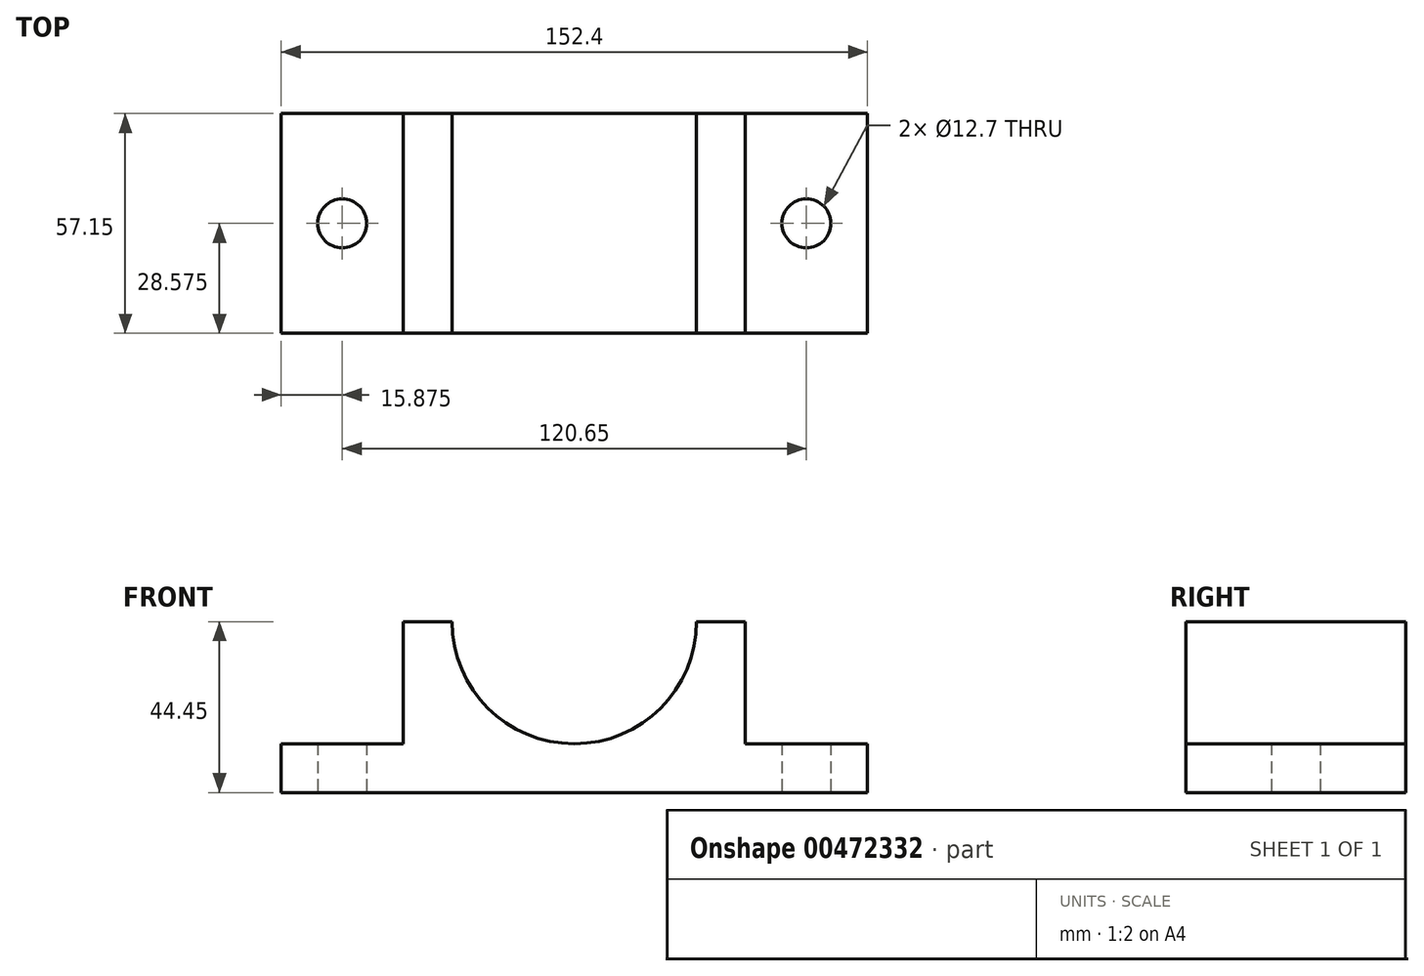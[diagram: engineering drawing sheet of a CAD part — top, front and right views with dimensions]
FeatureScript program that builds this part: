
annotation { "Feature Type Name" : "Feature", "Feature Type Description" : "" }
export const myFeature = defineFeature(function(context is Context, id is Id, definition is map)
    precondition{}
    {
        {
            var Q0;
            Q0=qCreatedBy(makeId("Front.planeOp"),FACE);
            var sketch = newSketch(context, id + "F0", { "sketchPlane" : qUnion([Q0])});
            skLineSegment(sketch, "E0", {"start": v(0, 0) * mm, "end": v(76.2, 0) * mm});
            skLineSegment(sketch, "E1", {"start": v(0, 0) * mm, "end": v(-76.2, 0) * mm});
            skLineSegment(sketch, "E2", {"start": v(76.2, 0) * mm, "end": v(76.2, 12.7) * mm});
            skLineSegment(sketch, "E3", {"start": v(-76.2, 0) * mm, "end": v(-76.2, 12.7) * mm});
            skLineSegment(sketch, "E4", {"start": v(-76.2, 12.7) * mm, "end": v(-44.45, 12.7) * mm});
            skLineSegment(sketch, "E5", {"start": v(76.2, 12.7) * mm, "end": v(44.45, 12.7) * mm});
            skLineSegment(sketch, "E6", {"start": v(-44.45, 12.7) * mm, "end": v(-44.45, 44.45) * mm});
            skLineSegment(sketch, "E7", {"start": v(44.45, 12.7) * mm, "end": v(44.45, 44.45) * mm});
            skCircle(sketch, "E8", {"center": v(0, 44.45) * mm, "radius": 31.75 * mm});
            skLineSegment(sketch, "E9", {"start": v(44.45, 44.45) * mm, "end": v(31.75, 44.45) * mm});
            skLineSegment(sketch, "E10", {"start": v(-44.45, 44.45) * mm, "end": v(-31.75, 44.45) * mm});
            skSolve(sketch);
        }
        {
            var Q0;
            Q0=makeQuery(id+"F0.imprint","IMPRINT",FACE,{"disambiguationData":[TD([[makeQuery(id+"F0.imprint","IMPRINT",EDGE,{"derivedFrom":sQuery(id+"F0.wireOp",EDGE,"E0")}),1.0]])]});
            extrude(context, id + "F1", {"entities" : qUnion([Q0]), "depth" : 57.15 * mm});
        }
        {
            var Q0;
            Q0=qCreatedBy(makeId("Top.planeOp"),FACE);
            var sketch = newSketch(context, id + "F2", { "sketchPlane" : qUnion([Q0])});
            skLineSegment(sketch, "E11", {"start": v(-60.33, -57.15) * mm, "end": v(-60.33, 0) * mm, "construction": true});
            skLineSegment(sketch, "E12", {"start": v(60.33, -57.15) * mm, "end": v(60.33, 0) * mm, "construction": true});
            skCircle(sketch, "E13", {"center": v(-60.33, -28.58) * mm, "radius": 6.35 * mm});
            skCircle(sketch, "E14", {"center": v(60.33, -28.58) * mm, "radius": 6.35 * mm});
            skSolve(sketch);
        }
        {
            var Q0;
            Q0 = qSketchRegion(id + "F2", true);
            extrude(context, id + "F3", {"entities" : qUnion([Q0]), "operationType" : NewBodyOperationType.REMOVE, "depth" : 25.4 * mm});
        }
    });
